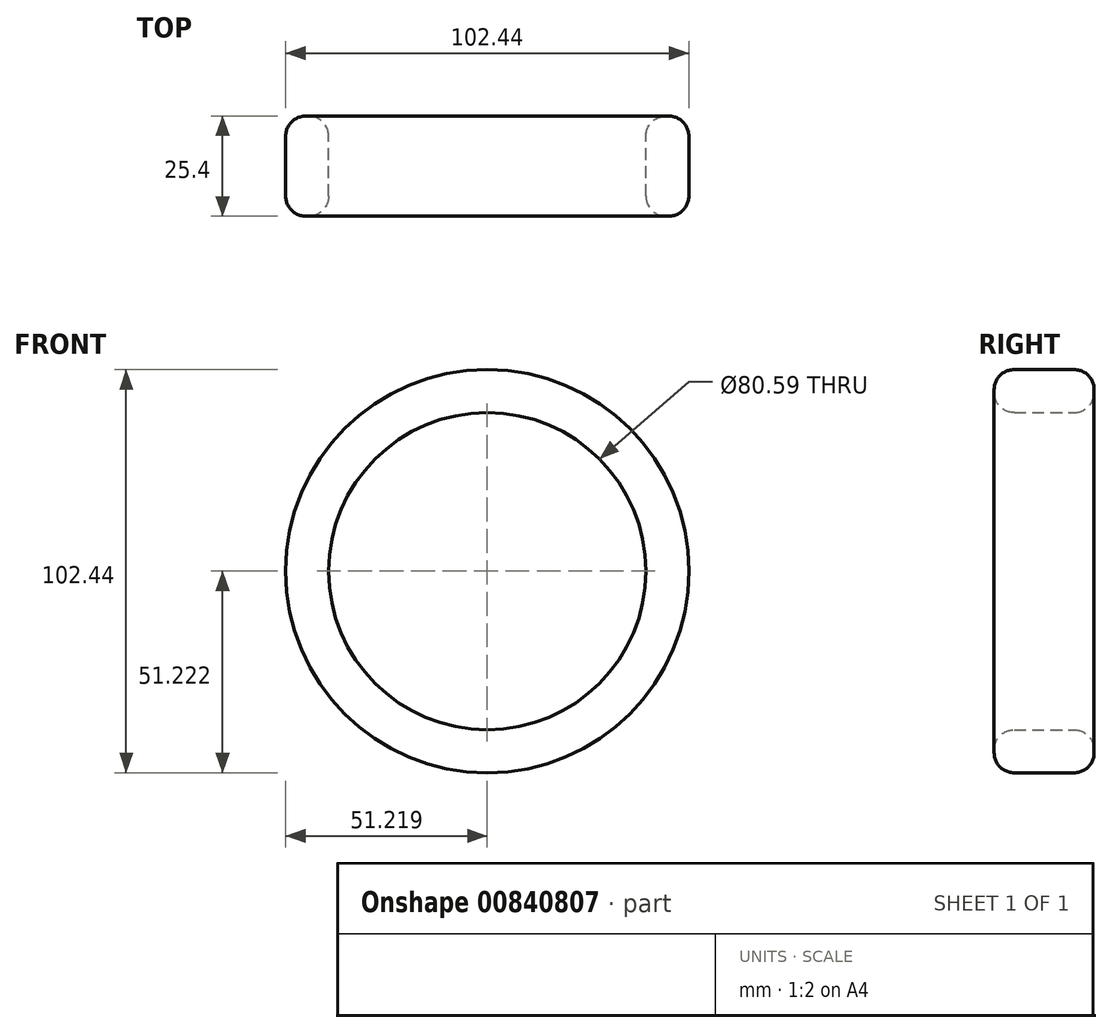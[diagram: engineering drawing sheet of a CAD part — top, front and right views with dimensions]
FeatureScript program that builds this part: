
annotation { "Feature Type Name" : "Feature", "Feature Type Description" : "" }
export const myFeature = defineFeature(function(context is Context, id is Id, definition is map)
    precondition{}
    {
        {
            var Q0;
            Q0=qCreatedBy(makeId("Front.planeOp"),FACE);
            var sketch = newSketch(context, id + "F0", { "sketchPlane" : qUnion([Q0])});
            skCircle(sketch, "E0", {"center": v(-93.01, 45.48) * mm, "radius": 51.22 * mm});
            skCircle(sketch, "E1", {"center": v(-93.01, 45.48) * mm, "radius": 40.3 * mm});
            skSolve(sketch);
        }
        {
            var Q0;
            Q0 = qSketchRegion(id + "F0", true);
            extrude(context, id + "F1", {"entities" : qUnion([Q0]), "depth" : 25.4 * mm, "offsetDistance" : 25.4 * mm});
        }
        {
            var Q0;
            Q0=makeQuery(id+"F1.opExtrude","CAP_EDGE",EDGE,{"disambiguationData":[OSD([sQuery(id+"F0.wireOp",EDGE,"E0")])],"isStart":false});
            var Q1;
            Q1=makeQuery(id+"F1.opExtrude","CAP_EDGE",EDGE,{"disambiguationData":[OSD([sQuery(id+"F0.wireOp",EDGE,"E0")])],"isStart":true});
            fillet(context, id + "F2", {"entities" : qUnion([Q0, Q1]), "radius" : 5.08 * mm, "tangentPropagation" : true, "allowEdgeOverflow" : false});
        }
        {
            var Q0;
            Q0=makeQuery(id+"F1.opExtrude","CAP_EDGE",EDGE,{"disambiguationData":[OSD([sQuery(id+"F0.wireOp",EDGE,"E1")])],"isStart":false});
            fillet(context, id + "F3", {"entities" : qUnion([Q0]), "radius" : 5.08 * mm, "tangentPropagation" : true, "allowEdgeOverflow" : false});
        }
        {
            var Q0;
            Q0=makeQuery(id+"F1.opExtrude","CAP_EDGE",EDGE,{"disambiguationData":[OSD([sQuery(id+"F0.wireOp",EDGE,"E1")])],"isStart":true});
            fillet(context, id + "F4", {"entities" : qUnion([Q0]), "radius" : 5.08 * mm, "tangentPropagation" : true, "allowEdgeOverflow" : false});
        }
    });
